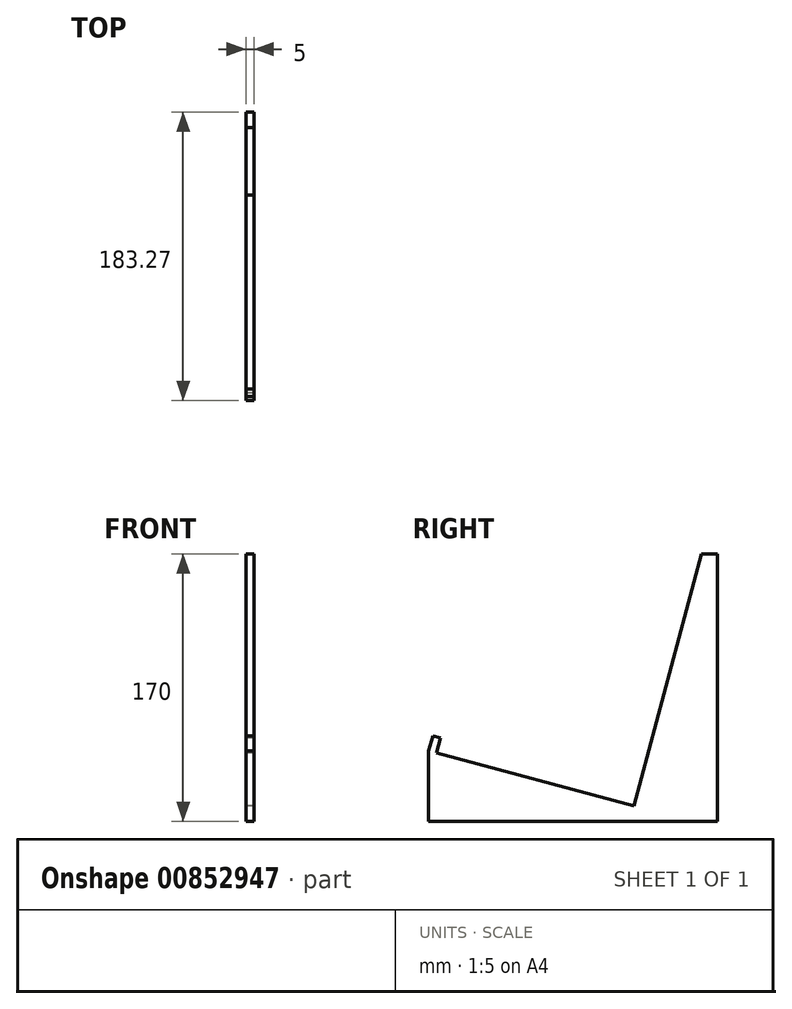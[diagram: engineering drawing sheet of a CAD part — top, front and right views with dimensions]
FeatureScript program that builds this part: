
annotation { "Feature Type Name" : "Feature", "Feature Type Description" : "" }
export const myFeature = defineFeature(function(context is Context, id is Id, definition is map)
    precondition{}
    {
        {
            var Q0;
            Q0=qCreatedBy(makeId("Right.planeOp"),FACE);
            var sketch = newSketch(context, id + "F0", { "sketchPlane" : qUnion([Q0])});
            skLineSegment(sketch, "E0", {"start": v(0, 0) * mm, "end": v(-125.57, 33.65) * mm});
            skLineSegment(sketch, "E1", {"start": v(-125.57, 33.65) * mm, "end": v(-125.57, 0) * mm, "construction": true});
            skLineSegment(sketch, "E2", {"start": v(-125.57, 0) * mm, "end": v(-125.57, -10) * mm});
            skLineSegment(sketch, "E3", {"start": v(-125.57, -10) * mm, "end": v(0, -10) * mm});
            skLineSegment(sketch, "E4", {"start": v(0, -10) * mm, "end": v(0, 0) * mm, "construction": true});
            skLineSegment(sketch, "E5", {"start": v(0, 0) * mm, "end": v(42.87, 160) * mm});
            skLineSegment(sketch, "E6", {"start": v(42.87, 160) * mm, "end": v(52.87, 160) * mm});
            skLineSegment(sketch, "E7", {"start": v(52.87, 160) * mm, "end": v(52.87, -10) * mm});
            skLineSegment(sketch, "E8", {"start": v(52.87, -10) * mm, "end": v(0, -10) * mm});
            skLineSegment(sketch, "E9", {"start": v(-125.57, 33.65) * mm, "end": v(-122.98, 43.3) * mm});
            skLineSegment(sketch, "E10", {"start": v(-122.98, 43.3) * mm, "end": v(-127.81, 44.6) * mm});
            skLineSegment(sketch, "E11", {"start": v(-127.81, 44.6) * mm, "end": v(-130.4, 34.94) * mm});
            skLineSegment(sketch, "E12", {"start": v(-125.57, -10) * mm, "end": v(-130.4, -10) * mm});
            skLineSegment(sketch, "E13", {"start": v(-130.4, -10) * mm, "end": v(-130.4, 34.94) * mm});
            skLineSegment(sketch, "E14", {"start": v(-125.57, 33.65) * mm, "end": v(-130.4, 34.94) * mm, "construction": true});
            skSolve(sketch);
        }
        {
            var Q0;
            Q0=makeQuery(id+"F0.imprint","IMPRINT",FACE,{"disambiguationData":[TD([[makeQuery(id+"F0.imprint","IMPRINT",EDGE,{"derivedFrom":sQuery(id+"F0.wireOp",EDGE,"E0")}),1.0]])]});
            extrude(context, id + "F1", {"entities" : qUnion([Q0]), "depth" : 5 * mm, "offsetDistance" : 25 * mm});
        }
    });
